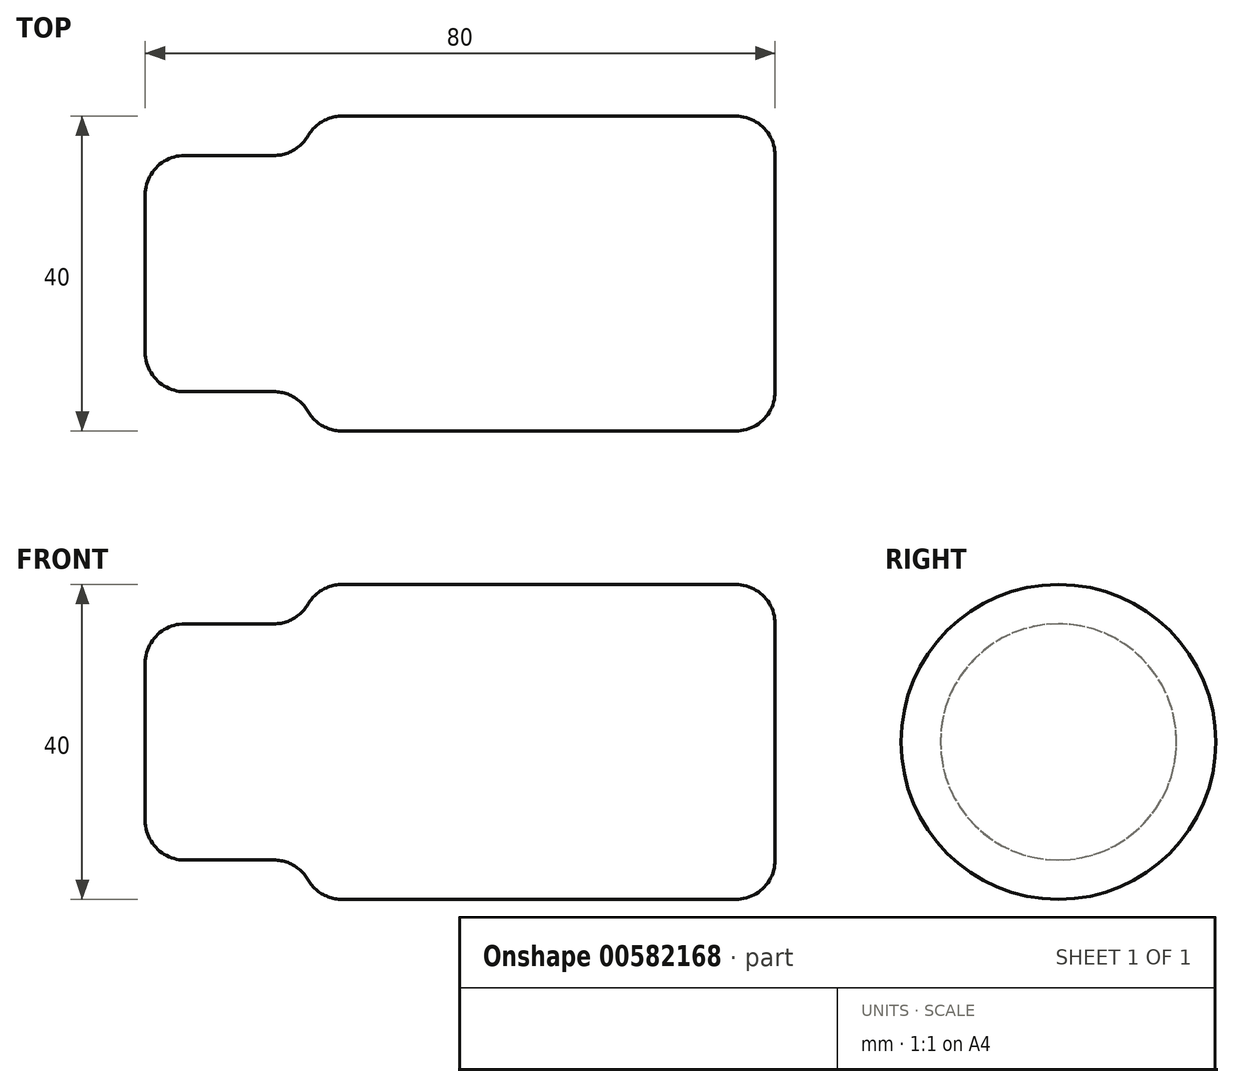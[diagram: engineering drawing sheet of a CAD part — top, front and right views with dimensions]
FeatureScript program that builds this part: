
annotation { "Feature Type Name" : "Feature", "Feature Type Description" : "" }
export const myFeature = defineFeature(function(context is Context, id is Id, definition is map)
    precondition{}
    {
        {
            var Q0;
            Q0=qCreatedBy(makeId("Front.planeOp"),FACE);
            var sketch = newSketch(context, id + "F0", { "sketchPlane" : qUnion([Q0])});
            skLineSegment(sketch, "E0.bottom", {"start": v(0, 0) * mm, "end": v(-60, 0) * mm});
            skLineSegment(sketch, "E0.top", {"start": v(0, 20) * mm, "end": v(-60, 20) * mm});
            skLineSegment(sketch, "E0.left", {"start": v(0, 0) * mm, "end": v(0, 20) * mm});
            skLineSegment(sketch, "E0.right", {"start": v(-60, 0) * mm, "end": v(-60, 20) * mm});
            skSolve(sketch);
        }
        {
            var Q0;
            Q0=makeQuery(id+"F0.imprint","IMPRINT",FACE,{"disambiguationData":[TD([[makeQuery(id+"F0.imprint","IMPRINT",EDGE,{"derivedFrom":sQuery(id+"F0.wireOp",EDGE,"E0.bottom")}),-1.0]])]});
            var Q1;
            Q1=sQuery(id+"F0.wireOp",EDGE,"E0.bottom");
            revolve(context, id + "F1", {"entities" : qUnion([Q0]), "axis" : qUnion([Q1]), "revolveType" : RevolveType.FULL});
        }
        {
            var Q0;
            Q0=makeQuery(id+"F1.opRevolve","SWEPT_FACE",FACE,{"disambiguationData":[OSD([sQuery(id+"F0.wireOp",EDGE,"E0.right")])]});
            var Q1;
            Q1=makeQuery(id+"F1.opRevolve","SWEPT_FACE",FACE,{"disambiguationData":[OSD([sQuery(id+"F0.wireOp",EDGE,"E0.left")])]});
            fillet(context, id + "F2", {"entities" : qUnion([Q0, Q1]), "radius" : 5 * mm, "tangentPropagation" : true, "allowEdgeOverflow" : false});
        }
        {
            var Q0;
            Q0=makeQuery(id+"F1.opRevolve","SWEPT_FACE",FACE,{"disambiguationData":[OSD([sQuery(id+"F0.wireOp",EDGE,"E0.right")])]});
            extrude(context, id + "F3", {"entities" : qUnion([Q0]), "operationType" : NewBodyOperationType.ADD, "depth" : 20 * mm, "offsetDistance" : 25 * mm});
        }
        {
            var Q0;
            {var subQ0=sQuery(id+"F0.wireOp",EDGE,"E0.right");var subQ1=sQuery(id+"F0.wireOp",EDGE,"E0.top");Q0=makeQuery(id+"F3.boolean.opBoolean","MERGE",EDGE,{"derivedFrom":[makeQuery(id+"F2.opFillet","BLEND_EDGE",EDGE,{"blendedFrom":[makeQuery(id+"F1.opRevolve","SWEPT_EDGE",EDGE,{"disambiguationData":[OSD([subQ1,subQ0])]}),makeQuery(id+"F1.opRevolve","SWEPT_FACE",FACE,{"disambiguationData":[OSD([subQ0])]})],"blendedInto":[makeQuery(id+"F1.opRevolve","SWEPT_FACE",FACE,{"disambiguationData":[OSD([subQ0])]})]}),makeQuery(id+"F3.opExtrude","CAP_EDGE",EDGE,{"disambiguationData":[OSD([subQ1,subQ0])],"isStart":true})]});}
            var Q1;
            Q1=makeQuery(id+"F3.opExtrude","CAP_FACE",FACE,{"disambiguationData":[OSD([sQuery(id+"F0.wireOp",EDGE,"E0.right")])],"isStart":false});
            fillet(context, id + "F4", {"entities" : qUnion([Q0, Q1]), "radius" : 5 * mm, "tangentPropagation" : true, "allowEdgeOverflow" : false});
        }
    });
